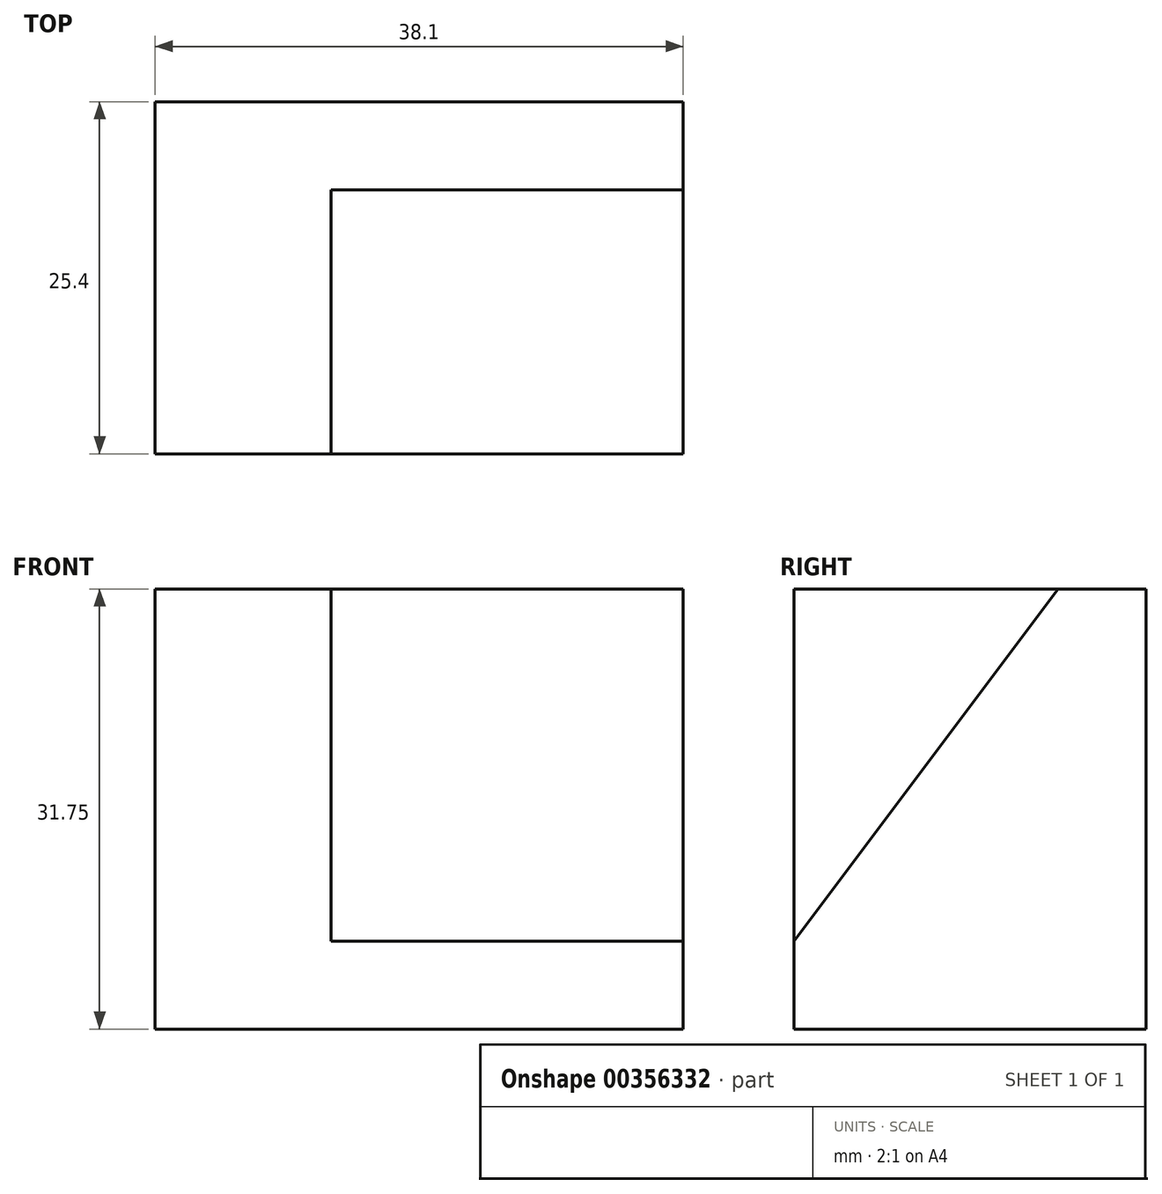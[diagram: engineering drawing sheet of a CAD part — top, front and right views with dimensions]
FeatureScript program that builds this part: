
annotation { "Feature Type Name" : "Feature", "Feature Type Description" : "" }
export const myFeature = defineFeature(function(context is Context, id is Id, definition is map)
    precondition{}
    {
        {
            var Q0;
            Q0=qCreatedBy(makeId("Front.planeOp"),FACE);
            var sketch = newSketch(context, id + "F0", { "sketchPlane" : qUnion([Q0])});
            skLineSegment(sketch, "E0", {"start": v(0, 0) * mm, "end": v(12.7, 0) * mm});
            skLineSegment(sketch, "E1", {"start": v(12.7, 0) * mm, "end": v(12.7, 31.75) * mm});
            skLineSegment(sketch, "E2", {"start": v(12.7, 31.75) * mm, "end": v(0, 31.75) * mm});
            skLineSegment(sketch, "E3", {"start": v(0, 31.75) * mm, "end": v(0, 0) * mm});
            skSolve(sketch);
        }
        {
            var Q0;
            Q0=makeQuery(id+"F0.imprint","IMPRINT",FACE,{"disambiguationData":[TD([[makeQuery(id+"F0.imprint","IMPRINT",EDGE,{"derivedFrom":sQuery(id+"F0.wireOp",EDGE,"E0")}),1.0]])]});
            extrude(context, id + "F1", {"entities" : qUnion([Q0]), "depth" : 25.4 * mm});
        }
        {
            var Q0;
            Q0=makeQuery(id+"F1.opExtrude","SWEPT_FACE",FACE,{"disambiguationData":[OSD([sQuery(id+"F0.wireOp",EDGE,"E1")])]});
            var sketch = newSketch(context, id + "F2", { "sketchPlane" : qUnion([Q0])});
            skLineSegment(sketch, "E4", {"start": v(-25.4, 0) * mm, "end": v(-25.4, 6.35) * mm});
            skLineSegment(sketch, "E5", {"start": v(-25.4, 6.35) * mm, "end": v(-6.35, 31.75) * mm});
            skLineSegment(sketch, "E6", {"start": v(-6.35, 31.75) * mm, "end": v(0, 31.75) * mm});
            skLineSegment(sketch, "E7", {"start": v(0, 31.75) * mm, "end": v(0, 0) * mm});
            skLineSegment(sketch, "E8", {"start": v(0, 0) * mm, "end": v(-25.4, 0) * mm});
            skSolve(sketch);
        }
        {
            var Q0;
            Q0=makeQuery(id+"F2.imprint","IMPRINT",FACE,{"disambiguationData":[TD([[makeQuery(id+"F2.imprint","IMPRINT",EDGE,{"derivedFrom":sQuery(id+"F2.wireOp",EDGE,"E4")}),-1.0]])]});
            extrude(context, id + "F3", {"entities" : qUnion([Q0]), "operationType" : NewBodyOperationType.ADD, "depth" : 25.4 * mm});
        }
    });
